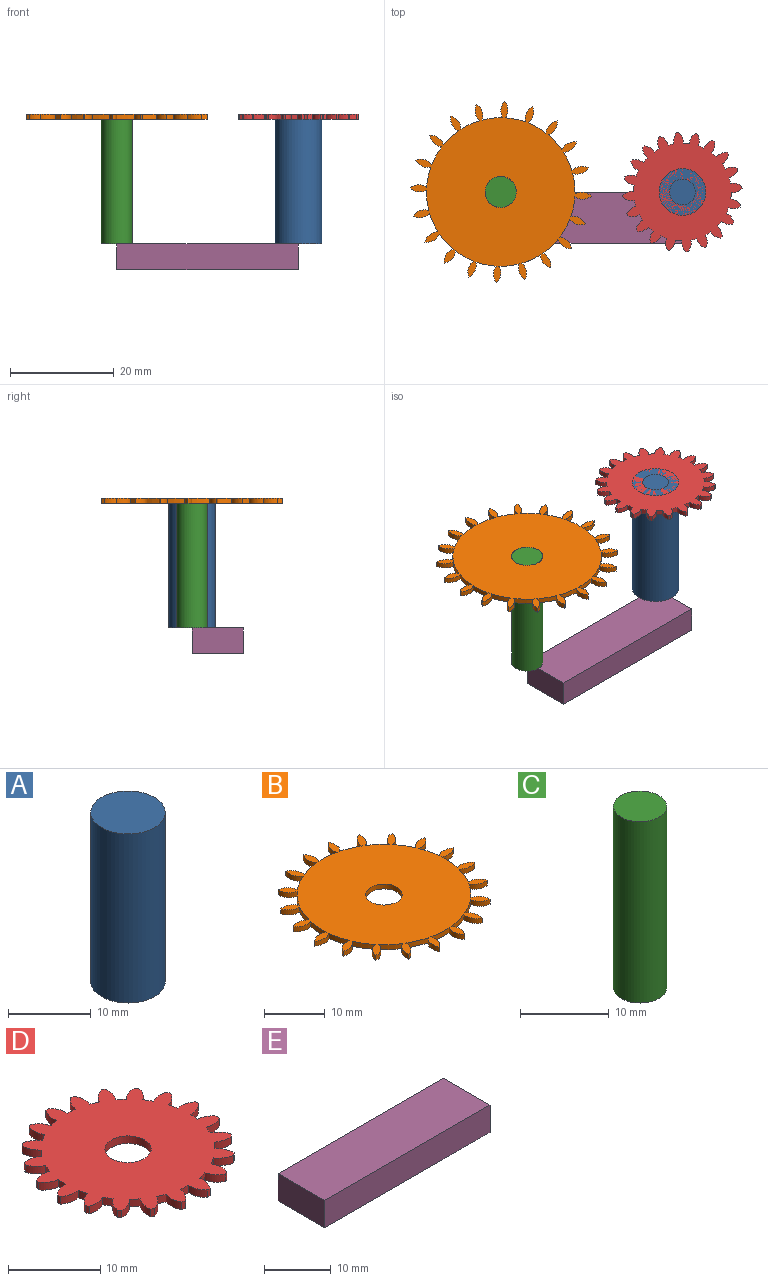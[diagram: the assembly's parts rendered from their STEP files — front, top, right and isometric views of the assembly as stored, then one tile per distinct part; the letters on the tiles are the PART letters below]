
ASSEMBLY  parts=5 mates=4
PART A: 3 faces, bbox 9x9x25 mm
  f0: cylinder r=4.5mm len=25mm, axis (0,0,-1), area 706.9mm2, adj f1,f2
  f1: plane 9x9mm, normal (0,0,1), area 63.6mm2, adj f0
  f2: plane 9x9mm, normal (0,0,-1), area 63.6mm2, adj f0
PART B: 63 faces, bbox 34.9x34.9x1 mm
  f0: cylinder r=2.61mm len=3.2mm, axis (0,0,-1), area 3.4mm2, adj f1,f59,f61,f62
  f1: cylinder r=14.32mm len=3.84mm, axis (0,0,-1), area 4mm2, adj f0,f2,f61,f62
  f2: cylinder r=2.61mm len=2.84mm, axis (0,0,-1), area 3.4mm2, adj f1,f3,f61,f62
  f3: cylinder r=2.61mm len=3.04mm, axis (0,0,-1), area 3.4mm2, adj f2,f4,f61,f62
  f4: cylinder r=14.32mm len=3.37mm, axis (0,0,-1), area 4mm2, adj f3,f5,f61,f62
  f5: cylinder r=2.61mm len=2.27mm, axis (0,0,-1), area 3.4mm2, adj f4,f6,f61,f62
  f6: cylinder r=2.61mm len=2.6mm, axis (0,0,-1), area 3.4mm2, adj f5,f7,f61,f62
  f7: cylinder r=14.32mm len=3mm, axis (0,0,-1), area 4mm2, adj f6,f8,f61,f62
  f8: cylinder r=2.61mm len=2.86mm, axis (0,0,-1), area 3.4mm2, adj f7,f9,f61,f62
  f9: cylinder r=2.61mm len=2.58mm, axis (0,0,-1), area 3.4mm2, adj f8,f10,f61,f62
  f10: cylinder r=14.32mm len=3.65mm, axis (0,0,-1), area 4mm2, adj f9,f11,f61,f62
  f11: cylinder r=2.61mm len=3.16mm, axis (0,0,-1), area 3.4mm2, adj f10,f12,f61,f62
  f12: cylinder r=2.61mm len=3.03mm, axis (0,0,-1), area 3.4mm2, adj f11,f13,f61,f62
  f13: cylinder r=14.32mm len=3.94mm, axis (0,0,-1), area 4mm2, adj f12,f14,f61,f62
  f14: cylinder r=2.61mm len=3.15mm, axis (0,0,-1), area 3.4mm2, adj f13,f15,f61,f62
  f15: cylinder r=2.61mm len=3.2mm, axis (0,0,-1), area 3.4mm2, adj f14,f16,f61,f62
  f16: cylinder r=14.32mm len=3.84mm, axis (0,0,-1), area 4mm2, adj f15,f17,f61,f62
  f17: cylinder r=2.61mm len=2.84mm, axis (0,0,-1), area 3.4mm2, adj f16,f18,f61,f62
  f18: cylinder r=2.61mm len=3.04mm, axis (0,0,-1), area 3.4mm2, adj f17,f19,f61,f62
  f19: cylinder r=14.32mm len=3.37mm, axis (0,0,-1), area 4mm2, adj f18,f20,f61,f62
  f20: cylinder r=2.61mm len=2.27mm, axis (0,0,-1), area 3.4mm2, adj f19,f21,f61,f62
  f21: cylinder r=2.61mm len=2.6mm, axis (0,0,-1), area 3.4mm2, adj f20,f22,f61,f62
  f22: cylinder r=14.32mm len=3mm, axis (0,0,-1), area 4mm2, adj f21,f23,f61,f62
  f23: cylinder r=2.61mm len=2.86mm, axis (0,0,-1), area 3.4mm2, adj f22,f24,f61,f62
  f24: cylinder r=2.61mm len=2.58mm, axis (0,0,-1), area 3.4mm2, adj f23,f25,f61,f62
  f25: cylinder r=14.32mm len=3.65mm, axis (0,0,-1), area 4mm2, adj f24,f26,f61,f62
  f26: cylinder r=2.61mm len=3.16mm, axis (0,0,-1), area 3.4mm2, adj f25,f27,f61,f62
  f27: cylinder r=2.61mm len=3.03mm, axis (0,0,-1), area 3.4mm2, adj f26,f28,f61,f62
  f28: cylinder r=14.32mm len=3.94mm, axis (0,0,-1), area 4mm2, adj f27,f29,f61,f62
  f29: cylinder r=2.61mm len=3.15mm, axis (0,0,-1), area 3.4mm2, adj f28,f30,f61,f62
  f30: cylinder r=2.61mm len=3.2mm, axis (0,0,-1), area 3.4mm2, adj f29,f31,f61,f62
  f31: cylinder r=14.32mm len=3.84mm, axis (0,0,-1), area 4mm2, adj f30,f32,f61,f62
  f32: cylinder r=2.61mm len=2.84mm, axis (0,0,-1), area 3.4mm2, adj f31,f33,f61,f62
  f33: cylinder r=2.61mm len=3.04mm, axis (0,0,-1), area 3.4mm2, adj f32,f34,f61,f62
  f34: cylinder r=14.32mm len=3.37mm, axis (0,0,-1), area 4mm2, adj f33,f35,f61,f62
  f35: cylinder r=2.61mm len=2.27mm, axis (0,0,-1), area 3.4mm2, adj f34,f36,f61,f62
  f36: cylinder r=2.61mm len=2.6mm, axis (0,0,-1), area 3.4mm2, adj f35,f37,f61,f62
  f37: cylinder r=14.32mm len=3mm, axis (0,0,-1), area 4mm2, adj f36,f38,f61,f62
  f38: cylinder r=2.61mm len=2.86mm, axis (0,0,-1), area 3.4mm2, adj f37,f39,f61,f62
  f39: cylinder r=2.61mm len=2.58mm, axis (0,0,-1), area 3.4mm2, adj f38,f40,f61,f62
  f40: cylinder r=14.32mm len=3.65mm, axis (0,0,-1), area 4mm2, adj f39,f41,f61,f62
  f41: cylinder r=2.61mm len=3.16mm, axis (0,0,-1), area 3.4mm2, adj f40,f42,f61,f62
  f42: cylinder r=2.61mm len=3.03mm, axis (0,0,-1), area 3.4mm2, adj f41,f43,f61,f62
  f43: cylinder r=14.32mm len=3.94mm, axis (0,0,-1), area 4mm2, adj f42,f44,f61,f62
  f44: cylinder r=2.61mm len=3.15mm, axis (0,0,-1), area 3.4mm2, adj f43,f45,f61,f62
  f45: cylinder r=2.61mm len=3.2mm, axis (0,0,-1), area 3.4mm2, adj f44,f46,f61,f62
  f46: cylinder r=14.32mm len=3.84mm, axis (0,0,-1), area 4mm2, adj f45,f47,f61,f62
  f47: cylinder r=2.61mm len=2.84mm, axis (0,0,-1), area 3.4mm2, adj f46,f48,f61,f62
  f48: cylinder r=2.61mm len=3.04mm, axis (0,0,-1), area 3.4mm2, adj f47,f49,f61,f62
  f49: cylinder r=14.32mm len=3.37mm, axis (0,0,-1), area 4mm2, adj f48,f50,f61,f62
  f50: cylinder r=2.61mm len=2.27mm, axis (0,0,-1), area 3.4mm2, adj f49,f51,f61,f62
  f51: cylinder r=2.61mm len=2.6mm, axis (0,0,-1), area 3.4mm2, adj f50,f52,f61,f62
  f52: cylinder r=14.32mm len=3mm, axis (0,0,-1), area 4mm2, adj f51,f53,f61,f62
  f53: cylinder r=2.61mm len=2.86mm, axis (0,0,-1), area 3.4mm2, adj f52,f54,f61,f62
  f54: cylinder r=2.61mm len=2.58mm, axis (0,0,-1), area 3.4mm2, adj f53,f55,f61,f62
  f55: cylinder r=14.32mm len=3.65mm, axis (0,0,-1), area 4mm2, adj f54,f56,f61,f62
  f56: cylinder r=2.61mm len=3.16mm, axis (0,0,-1), area 3.4mm2, adj f55,f57,f61,f62
  f57: cylinder r=2.61mm len=3.03mm, axis (0,0,-1), area 3.4mm2, adj f56,f58,f61,f62
  f58: cylinder r=14.32mm len=3.94mm, axis (0,0,-1), area 4mm2, adj f57,f59,f61,f62
  f59: cylinder r=2.61mm len=3.15mm, axis (0,0,-1), area 3.4mm2, adj f0,f58,f61,f62
  f60: cylinder r=3mm len=6mm, axis (0,0,-1), area 18.8mm2, adj f61,f62
  f61: plane 34.89x34.89mm, normal (0,0,1), area 680.4mm2, adj f0,f1,f2,f3,f4,f5,f6,f7
  f62: plane 34.89x34.89mm, normal (0,0,-1), area 680.4mm2, adj f0,f1,f2,f3,f4,f5,f6,f7
PART C: 3 faces, bbox 6x6x25 mm
  f0: cylinder r=3mm len=25mm, axis (0,0,-1), area 471.2mm2, adj f1,f2
  f1: plane 6x6mm, normal (0,0,1), area 28.3mm2, adj f0
  f2: plane 6x6mm, normal (0,0,-1), area 28.3mm2, adj f0
PART D: 83 faces, bbox 23x23x1 mm
  f0: cylinder r=2.61mm len=2.18mm, axis (0,0,-1), area 2.3mm2, adj f1,f79,f81,f82
  f1: cylinder r=9.41mm len=1.14mm, axis (0,0,-1), area 1.2mm2, adj f0,f2,f81,f82
  f2: cylinder r=2.61mm len=1.71mm, axis (0,0,-1), area 2.3mm2, adj f1,f3,f81,f82
  f3: plane 1x0.41mm, normal (-0.38,0.92,0), area 0.4mm2, adj f2,f4,f81,f82
  f4: cylinder r=2.61mm len=2.23mm, axis (0,0,-1), area 2.3mm2, adj f3,f5,f81,f82
  f5: cylinder r=9.41mm len=1mm, axis (0,0,-1), area 1.2mm2, adj f4,f6,f81,f82
  f6: cylinder r=2.61mm len=1.89mm, axis (0,0,-1), area 2.3mm2, adj f5,f7,f81,f82
  f7: plane 1x0.34mm, normal (-0.65,0.76,0), area 0.4mm2, adj f6,f8,f81,f82
  f8: cylinder r=2.61mm len=2.06mm, axis (0,0,-1), area 2.3mm2, adj f7,f9,f81,f82
  f9: cylinder r=9.41mm len=1mm, axis (0,0,-1), area 1.2mm2, adj f8,f10,f81,f82
  f10: cylinder r=2.61mm len=2.17mm, axis (0,0,-1), area 2.3mm2, adj f9,f11,f81,f82
  f11: plane 1x0.38mm, normal (-0.85,0.52,0), area 0.4mm2, adj f10,f12,f81,f82
  f12: cylinder r=2.61mm len=1.68mm, axis (0,0,-1), area 2.3mm2, adj f11,f13,f81,f82
  f13: cylinder r=9.41mm len=1.08mm, axis (0,0,-1), area 1.2mm2, adj f12,f14,f81,f82
  f14: cylinder r=2.61mm len=2.23mm, axis (0,0,-1), area 2.3mm2, adj f13,f15,f81,f82
  f15: plane 1x0.43mm, normal (-0.97,0.23,0), area 0.4mm2, adj f14,f16,f81,f82
  f16: cylinder r=2.61mm len=1.92mm, axis (0,0,-1), area 2.3mm2, adj f15,f17,f81,f82
  f17: cylinder r=9.41mm len=1.17mm, axis (0,0,-1), area 1.2mm2, adj f16,f18,f81,f82
  f18: cylinder r=2.61mm len=2.07mm, axis (0,0,-1), area 2.3mm2, adj f17,f19,f81,f82
  f19: plane 1x0.44mm, normal (-1,-0.08,0), area 0.4mm2, adj f18,f20,f81,f82
  f20: cylinder r=2.61mm len=2.18mm, axis (0,0,-1), area 2.3mm2, adj f19,f21,f81,f82
  f21: cylinder r=9.41mm len=1.14mm, axis (0,0,-1), area 1.2mm2, adj f20,f22,f81,f82
  f22: cylinder r=2.61mm len=1.71mm, axis (0,0,-1), area 2.3mm2, adj f21,f23,f81,f82
  f23: plane 1x0.41mm, normal (-0.92,-0.38,0), area 0.4mm2, adj f22,f24,f81,f82
  f24: cylinder r=2.61mm len=2.23mm, axis (0,0,-1), area 2.3mm2, adj f23,f25,f81,f82
  f25: cylinder r=9.41mm len=1mm, axis (0,0,-1), area 1.2mm2, adj f24,f26,f81,f82
  f26: cylinder r=2.61mm len=1.89mm, axis (0,0,-1), area 2.3mm2, adj f25,f27,f81,f82
  f27: plane 1x0.34mm, normal (-0.76,-0.65,0), area 0.4mm2, adj f26,f28,f81,f82
  f28: cylinder r=2.61mm len=2.06mm, axis (0,0,-1), area 2.3mm2, adj f27,f29,f81,f82
  f29: cylinder r=9.41mm len=1mm, axis (0,0,-1), area 1.2mm2, adj f28,f30,f81,f82
  f30: cylinder r=2.61mm len=2.17mm, axis (0,0,-1), area 2.3mm2, adj f29,f31,f81,f82
  f31: plane 1x0.38mm, normal (-0.52,-0.85,0), area 0.4mm2, adj f30,f32,f81,f82
  f32: cylinder r=2.61mm len=1.68mm, axis (0,0,-1), area 2.3mm2, adj f31,f33,f81,f82
  f33: cylinder r=9.41mm len=1.08mm, axis (0,0,-1), area 1.2mm2, adj f32,f34,f81,f82
  f34: cylinder r=2.61mm len=2.23mm, axis (0,0,-1), area 2.3mm2, adj f33,f35,f81,f82
  f35: plane 1x0.43mm, normal (-0.23,-0.97,0), area 0.4mm2, adj f34,f36,f81,f82
  f36: cylinder r=2.61mm len=1.92mm, axis (0,0,-1), area 2.3mm2, adj f35,f37,f81,f82
  f37: cylinder r=9.41mm len=1.17mm, axis (0,0,-1), area 1.2mm2, adj f36,f38,f81,f82
  f38: cylinder r=2.61mm len=2.07mm, axis (0,0,-1), area 2.3mm2, adj f37,f39,f81,f82
  f39: plane 1x0.44mm, normal (0.08,-1,0), area 0.4mm2, adj f38,f40,f81,f82
  f40: cylinder r=2.61mm len=2.18mm, axis (0,0,-1), area 2.3mm2, adj f39,f41,f81,f82
  f41: cylinder r=9.41mm len=1.14mm, axis (0,0,-1), area 1.2mm2, adj f40,f42,f81,f82
  f42: cylinder r=2.61mm len=1.71mm, axis (0,0,-1), area 2.3mm2, adj f41,f43,f81,f82
  f43: plane 1x0.41mm, normal (0.38,-0.92,0), area 0.4mm2, adj f42,f44,f81,f82
  f44: cylinder r=2.61mm len=2.23mm, axis (0,0,-1), area 2.3mm2, adj f43,f45,f81,f82
  f45: cylinder r=9.41mm len=1mm, axis (0,0,-1), area 1.2mm2, adj f44,f46,f81,f82
  f46: cylinder r=2.61mm len=1.89mm, axis (0,0,-1), area 2.3mm2, adj f45,f47,f81,f82
  f47: plane 1x0.34mm, normal (0.65,-0.76,0), area 0.4mm2, adj f46,f48,f81,f82
  f48: cylinder r=2.61mm len=2.06mm, axis (0,0,-1), area 2.3mm2, adj f47,f49,f81,f82
  f49: cylinder r=9.41mm len=1mm, axis (0,0,-1), area 1.2mm2, adj f48,f50,f81,f82
  f50: cylinder r=2.61mm len=2.17mm, axis (0,0,-1), area 2.3mm2, adj f49,f51,f81,f82
  f51: plane 1x0.38mm, normal (0.85,-0.52,0), area 0.4mm2, adj f50,f52,f81,f82
  f52: cylinder r=2.61mm len=1.68mm, axis (0,0,-1), area 2.3mm2, adj f51,f53,f81,f82
  f53: cylinder r=9.41mm len=1.08mm, axis (0,0,-1), area 1.2mm2, adj f52,f54,f81,f82
  f54: cylinder r=2.61mm len=2.23mm, axis (0,0,-1), area 2.3mm2, adj f53,f55,f81,f82
  f55: plane 1x0.43mm, normal (0.97,-0.23,0), area 0.4mm2, adj f54,f56,f81,f82
  f56: cylinder r=2.61mm len=1.92mm, axis (0,0,-1), area 2.3mm2, adj f55,f57,f81,f82
  f57: cylinder r=9.41mm len=1.17mm, axis (0,0,-1), area 1.2mm2, adj f56,f58,f81,f82
  f58: cylinder r=2.61mm len=2.07mm, axis (0,0,-1), area 2.3mm2, adj f57,f59,f81,f82
  f59: plane 1x0.44mm, normal (1,0.08,0), area 0.4mm2, adj f58,f60,f81,f82
  f60: cylinder r=2.61mm len=2.18mm, axis (0,0,-1), area 2.3mm2, adj f59,f61,f81,f82
  f61: cylinder r=9.41mm len=1.14mm, axis (0,0,-1), area 1.2mm2, adj f60,f62,f81,f82
  f62: cylinder r=2.61mm len=1.71mm, axis (0,0,-1), area 2.3mm2, adj f61,f63,f81,f82
  f63: plane 1x0.41mm, normal (0.92,0.38,0), area 0.4mm2, adj f62,f64,f81,f82
  f64: cylinder r=2.61mm len=2.23mm, axis (0,0,-1), area 2.3mm2, adj f63,f65,f81,f82
  f65: cylinder r=9.41mm len=1mm, axis (0,0,-1), area 1.2mm2, adj f64,f66,f81,f82
  f66: cylinder r=2.61mm len=1.89mm, axis (0,0,-1), area 2.3mm2, adj f65,f67,f81,f82
  f67: plane 1x0.34mm, normal (0.76,0.65,0), area 0.4mm2, adj f66,f68,f81,f82
  f68: cylinder r=2.61mm len=2.06mm, axis (0,0,-1), area 2.3mm2, adj f67,f69,f81,f82
  f69: cylinder r=9.41mm len=1mm, axis (0,0,-1), area 1.2mm2, adj f68,f70,f81,f82
  f70: cylinder r=2.61mm len=2.17mm, axis (0,0,-1), area 2.3mm2, adj f69,f71,f81,f82
  f71: plane 1x0.38mm, normal (0.52,0.85,0), area 0.4mm2, adj f70,f72,f81,f82
  f72: cylinder r=2.61mm len=1.68mm, axis (0,0,-1), area 2.3mm2, adj f71,f73,f81,f82
  f73: cylinder r=9.41mm len=1.08mm, axis (0,0,-1), area 1.2mm2, adj f72,f74,f81,f82
  f74: cylinder r=2.61mm len=2.23mm, axis (0,0,-1), area 2.3mm2, adj f73,f75,f81,f82
  f75: plane 1x0.43mm, normal (0.23,0.97,0), area 0.4mm2, adj f74,f76,f81,f82
  f76: cylinder r=2.61mm len=1.92mm, axis (0,0,-1), area 2.3mm2, adj f75,f77,f81,f82
  f77: cylinder r=9.41mm len=1.17mm, axis (0,0,-1), area 1.2mm2, adj f76,f78,f81,f82
  f78: cylinder r=2.61mm len=2.07mm, axis (0,0,-1), area 2.3mm2, adj f77,f79,f81,f82
  f79: plane 1x0.44mm, normal (-0.08,1,0), area 0.4mm2, adj f0,f78,f81,f82
  f80: cylinder r=2.5mm len=5mm, axis (0,0,-1), area 15.7mm2, adj f81,f82
  f81: plane 22.96x22.96mm, normal (0,0,1), area 320mm2, adj f0,f1,f2,f3,f4,f5,f6,f7
  f82: plane 22.96x22.96mm, normal (0,0,-1), area 320mm2, adj f0,f1,f2,f3,f4,f5,f6,f7
PART E: 6 faces, bbox 35x9.9x5 mm
  f0: plane 9.86x5mm, normal (1,0,0), area 49.3mm2, adj f1,f3,f4,f5
  f1: plane 35x5mm, normal (0,1,0), area 175mm2, adj f0,f2,f4,f5
  f2: plane 9.86x5mm, normal (-1,0,0), area 49.3mm2, adj f1,f3,f4,f5
  f3: plane 35x5mm, normal (0,-1,0), area 175mm2, adj f0,f2,f4,f5
  f4: plane 35x9.86mm, normal (0,0,1), area 345mm2, adj f0,f1,f2,f3
  f5: plane 35x9.86mm, normal (0,0,-1), area 345mm2, adj f0,f1,f2,f3
PLACE A t=(0,0,-25)mm
PLACE B rot(axis=(0,0,1),64.9deg) t=(-35,0,-1)mm
PLACE C t=(-7.3,0,-25)mm
PLACE D t=(0,0,-1)mm
PLACE E t=(0,-9.86,-30)mm
MATE revolute C.f0 <-> B.f1  axis (0,0,1) through (-35,0,0)mm
MATE revolute A.f0 <-> D.f1  axis (0,0,1) through (0,0,0)mm
MATE fastened E.f4 <-> A.f0  axis (0,0,1) through (0,0,-25)mm
MATE fastened C.f0 <-> E.f4  axis (0,0,-1) through (-35,0,-25)mm
